# Revit family: JSA_Tag_Structural_Column_Type_Mark
name_source: partatom
category: Structural Column Tags
revit_build: Autodesk Revit 2015 (Build: 20140903_1530(x64)
units: mm (PartAtom-declared; Revit-internal decimal feet)

## types (14) — shared parameters

## per-type parameters (varying)
| type | 000 | 045 | 045 Over | 045 Under | 090 | 135 | 135 Over | 135 Under | 225 | 225 Over | 225 Under | 315 | 315 Over | 315 Under |
| 045 Type Mark | No | Yes | No | No | No | No | No | No | No | No | No | No | No | No |
| 135 Type Mark | No | No | No | No | No | Yes | No | No | No | No | No | No | No | No |
| 225 Type Mark | No | No | No | No | No | No | No | No | Yes | No | No | No | No | No |
| 315 Type Mark | No | No | No | No | No | No | No | No | No | No | No | Yes | No | No |
| 000 Type Mark | Yes | No | No | No | No | No | No | No | No | No | No | No | No | No |
| 090 Type Mark | No | No | No | No | Yes | No | No | No | No | No | No | No | No | No |
| 045 Type Mark Under | No | No | No | Yes | No | No | No | No | No | No | No | No | No | No |
| 135 Type Mark Under | No | No | No | No | No | No | No | Yes | No | No | No | No | No | No |
| 225 Type Mark Under | No | No | No | No | No | No | No | No | No | No | Yes | No | No | No |
| 315 Type Mark Under | No | No | No | No | No | No | No | No | No | No | No | No | No | Yes |
| 045 Type Mark Over | No | No | Yes | No | No | No | No | No | No | No | No | No | No | No |
| 135 Type Mark Over | No | No | No | No | No | No | Yes | No | No | No | No | No | No | No |
| 225 Type Mark Over | No | No | No | No | No | No | No | No | No | Yes | No | No | No | No |
| 315 Type Mark Over | No | No | No | No | No | No | No | No | No | No | No | No | Yes | No |

## geometry (parser evidence)
native form markers: Blend x4
no freeform markers — native parametric forms only
